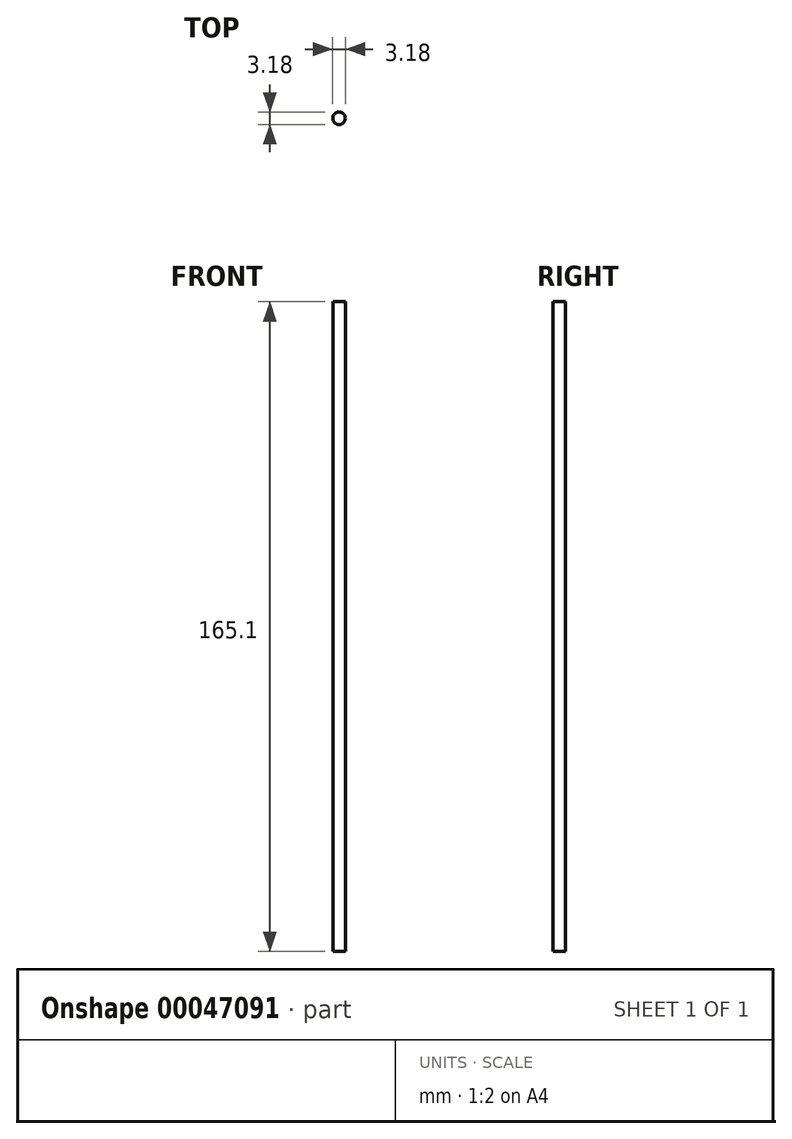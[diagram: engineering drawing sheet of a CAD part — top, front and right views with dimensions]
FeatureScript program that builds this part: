
annotation { "Feature Type Name" : "Feature", "Feature Type Description" : "" }
export const myFeature = defineFeature(function(context is Context, id is Id, definition is map)
    precondition{}
    {
        {
            var Q0;
            Q0=qCreatedBy(makeId("Top.planeOp"),FACE);
            var sketch = newSketch(context, id + "F0", { "sketchPlane" : qUnion([Q0])});
            skCircle(sketch, "E0", {"center": v(0, 0) * mm, "radius": 1.59 * mm});
            skSolve(sketch);
        }
        {
            var Q0;
            Q0 = qSketchRegion(id + "F0", true);
            extrude(context, id + "F1", {"entities" : qUnion([Q0]), "endBound" : BoundingType.SYMMETRIC, "depth" : 165.1 * mm});
        }
    });
